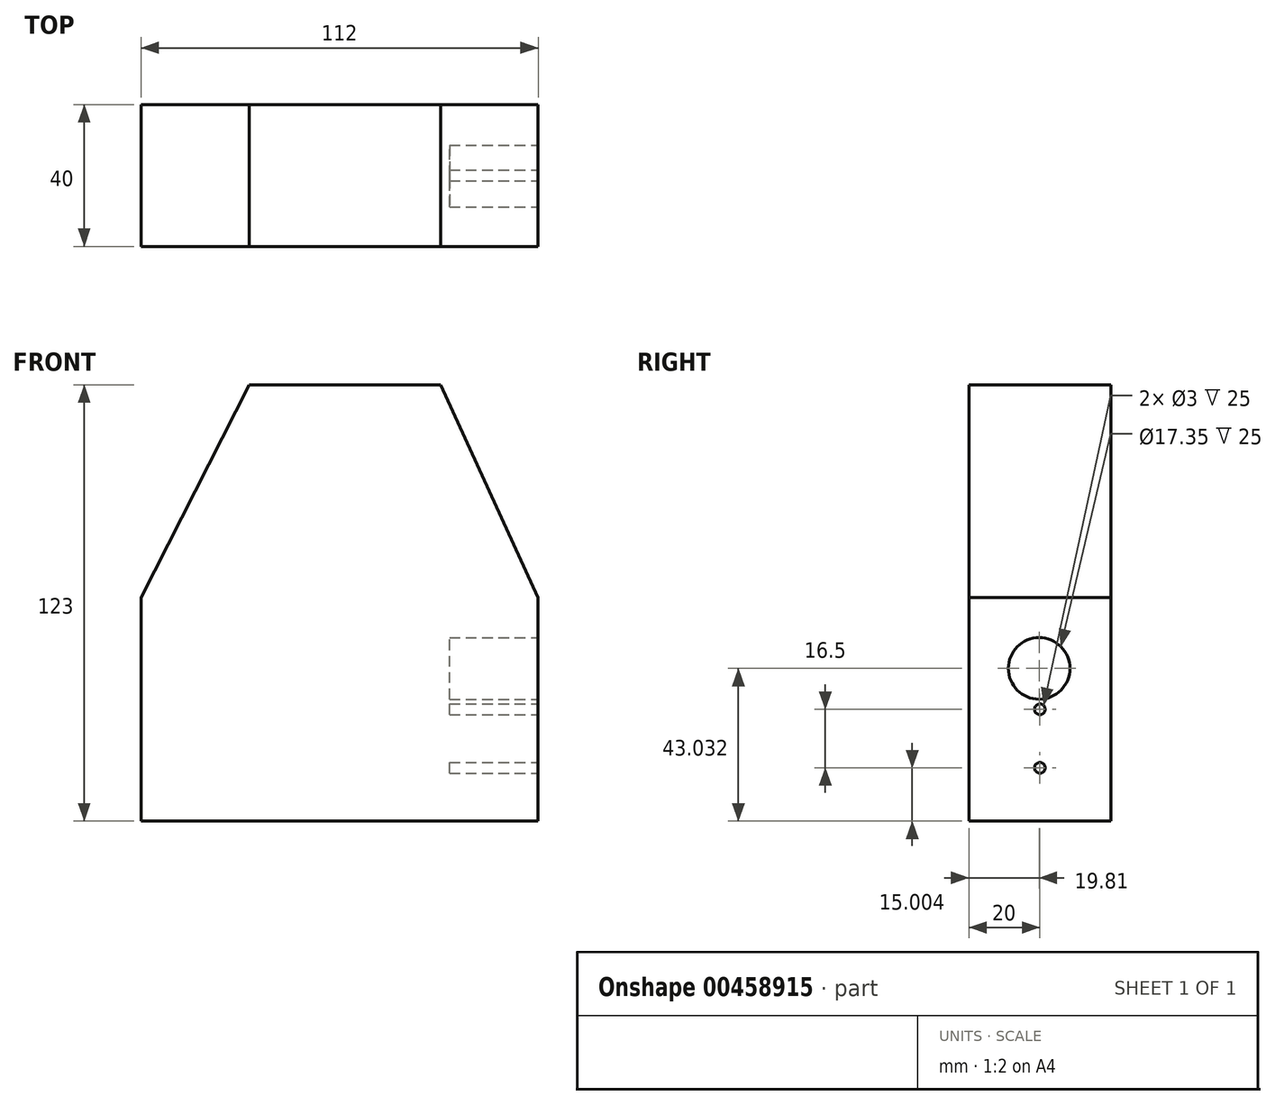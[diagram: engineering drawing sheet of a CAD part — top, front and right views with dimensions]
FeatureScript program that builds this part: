
annotation { "Feature Type Name" : "Feature", "Feature Type Description" : "" }
export const myFeature = defineFeature(function(context is Context, id is Id, definition is map)
    precondition{}
    {
        {
            var Q0;
            Q0=qCreatedBy(makeId("Front.planeOp"),FACE);
            var sketch = newSketch(context, id + "F0", { "sketchPlane" : qUnion([Q0])});
            skLineSegment(sketch, "E0.bottom", {"start": v(28, 2.1) * mm, "end": v(76.77, 2.1) * mm});
            skLineSegment(sketch, "E0.top", {"start": v(-2.58, -120.9) * mm, "end": v(109.42, -120.9) * mm});
            skLineSegment(sketch, "E0.left", {"start": v(-2.58, -57.9) * mm, "end": v(-2.58, -120.9) * mm});
            skLineSegment(sketch, "E0.right", {"start": v(109.42, -59.4) * mm, "end": v(109.42, -120.9) * mm});
            skLineSegment(sketch, "E1", {"start": v(28, 2.1) * mm, "end": v(-2.58, -57.9) * mm});
            skPoint(sketch, "E2.orphan", {"position": v(109.42, 2.1) * mm});
            skLineSegment(sketch, "E3", {"start": v(76.77, 2.1) * mm, "end": v(82, 2.1) * mm});
            skLineSegment(sketch, "E4", {"start": v(109.42, -57.9) * mm, "end": v(109.42, -59.4) * mm});
            skLineSegment(sketch, "E5", {"start": v(109.42, -57.9) * mm, "end": v(82, 2.1) * mm});
            skSolve(sketch);
        }
        {
            var Q0;
            Q0 = qSketchRegion(id + "F0", true);
            extrude(context, id + "F1", {"entities" : qUnion([Q0]), "depth" : 40 * mm});
        }
        {
            var Q0;
            Q0=makeQuery(id+"F1.opExtrude","SWEPT_FACE",FACE,{"disambiguationData":[OSD([sQuery(id+"F0.wireOp",EDGE,"E0.right"),sQuery(id+"F0.wireOp",EDGE,"E4")])]});
            var sketch = newSketch(context, id + "F2", { "sketchPlane" : qUnion([Q0])});
            skCircle(sketch, "E6", {"center": v(-20, -105.9) * mm, "radius": 1.5 * mm});
            skPoint(sketch, "E6.centerSnap0", {"position": v(-20, -120.9) * mm});
            skCircle(sketch, "E7", {"center": v(-20, -89.4) * mm, "radius": 1.5 * mm});
            skSolve(sketch);
        }
        {
            var Q0;
            Q0 = qSketchRegion(id + "F2", true);
            extrude(context, id + "F3", {"entities" : qUnion([Q0]), "operationType" : NewBodyOperationType.REMOVE, "oppositeDirection" : true, "depth" : 25 * mm});
        }
        {
            var Q0;
            Q0=makeQuery(id+"F1.opExtrude","SWEPT_FACE",FACE,{"disambiguationData":[OSD([sQuery(id+"F0.wireOp",EDGE,"E0.right"),sQuery(id+"F0.wireOp",EDGE,"E4")])]});
            var sketch = newSketch(context, id + "F4", { "sketchPlane" : qUnion([Q0])});
            skCircle(sketch, "E8", {"center": v(-20.19, -77.87) * mm, "radius": 8.67 * mm});
            skSolve(sketch);
        }
        {
            var Q0;
            Q0=makeQuery(id+"F4.imprint","IMPRINT",FACE,{"disambiguationData":[TD([[makeQuery(id+"F4.imprint","IMPRINT",EDGE,{"derivedFrom":sQuery(id+"F4.wireOp",EDGE,"E8")}),1.0]])]});
            extrude(context, id + "F5", {"entities" : qUnion([Q0]), "operationType" : NewBodyOperationType.REMOVE, "oppositeDirection" : true, "depth" : 25 * mm, "offsetDistance" : 25 * mm});
        }
    });
